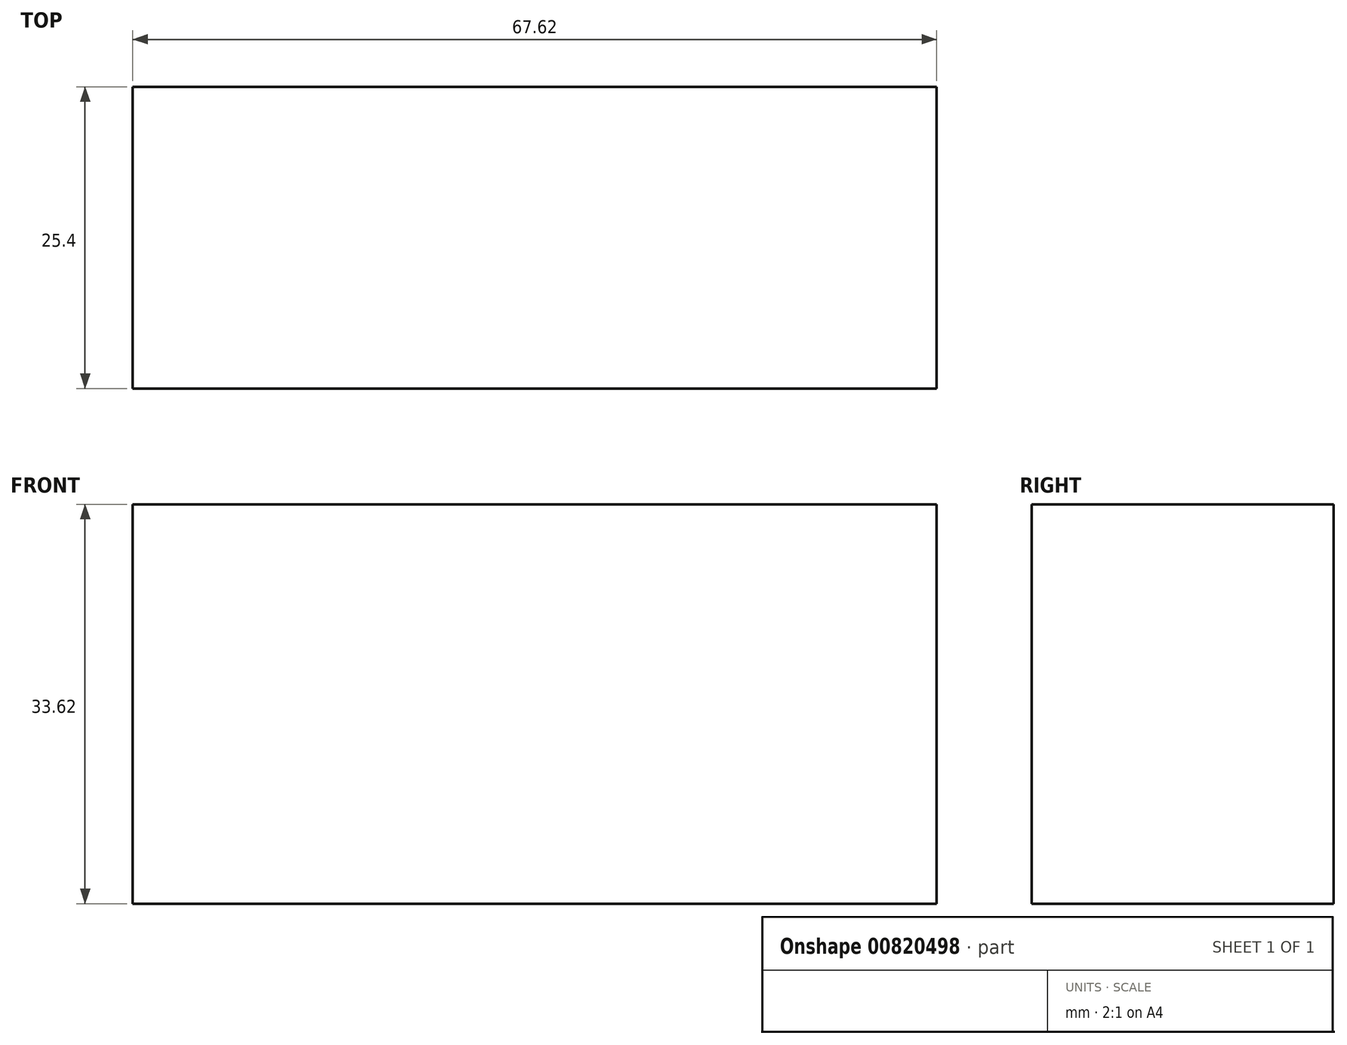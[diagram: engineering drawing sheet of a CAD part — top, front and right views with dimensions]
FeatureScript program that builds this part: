
annotation { "Feature Type Name" : "Feature", "Feature Type Description" : "" }
export const myFeature = defineFeature(function(context is Context, id is Id, definition is map)
    precondition{}
    {
        {
            var Q0;
            Q0=qCreatedBy(makeId("Front.planeOp"),FACE);
            var sketch = newSketch(context, id + "F0", { "sketchPlane" : qUnion([Q0])});
            skLineSegment(sketch, "E0.bottom", {"start": v(33.81, -16.81) * mm, "end": v(-33.81, -16.81) * mm});
            skLineSegment(sketch, "E0.top", {"start": v(33.81, 16.81) * mm, "end": v(-33.81, 16.81) * mm});
            skLineSegment(sketch, "E0.left", {"start": v(33.81, -16.81) * mm, "end": v(33.81, 16.81) * mm});
            skLineSegment(sketch, "E0.right", {"start": v(-33.81, -16.81) * mm, "end": v(-33.81, 16.81) * mm});
            skPoint(sketch, "E0.middle", {"position": v(0, 0) * mm});
            skSolve(sketch);
        }
        {
            var Q0;
            Q0=makeQuery(id+"F0.imprint","IMPRINT",FACE,{"disambiguationData":[TD([[makeQuery(id+"F0.imprint","IMPRINT",EDGE,{"derivedFrom":sQuery(id+"F0.wireOp",EDGE,"E0.bottom")}),-1.0]])]});
            extrude(context, id + "F1", {"entities" : qUnion([Q0]), "depth" : 25.4 * mm, "offsetDistance" : 25.4 * mm});
        }
    });
